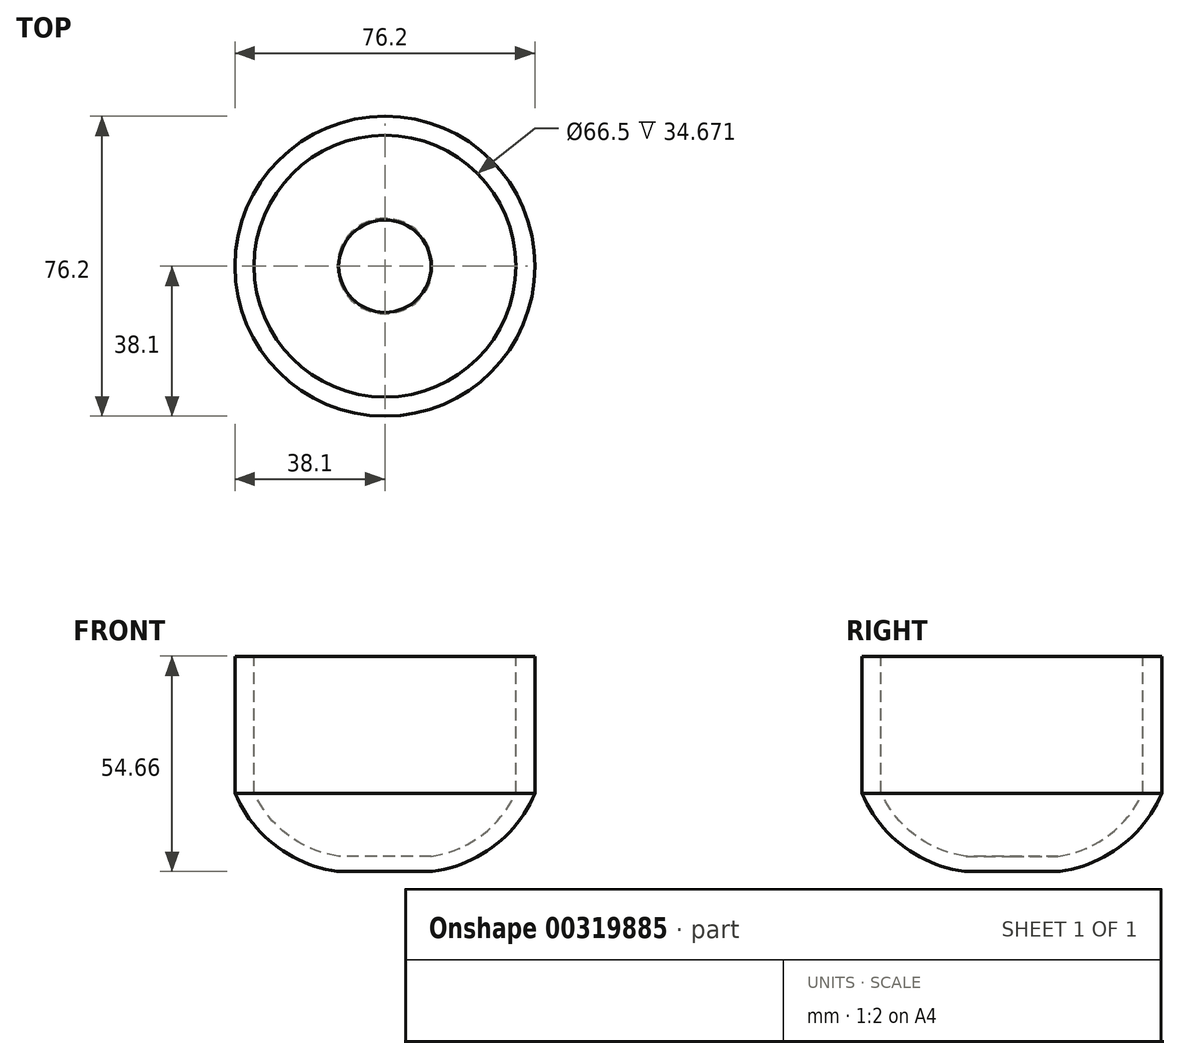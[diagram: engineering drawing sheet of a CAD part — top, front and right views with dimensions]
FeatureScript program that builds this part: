
annotation { "Feature Type Name" : "Feature", "Feature Type Description" : "" }
export const myFeature = defineFeature(function(context is Context, id is Id, definition is map)
    precondition{}
    {
        {
            var Q0;
            Q0=qCreatedBy(makeId("Front.planeOp"),FACE);
            var sketch = newSketch(context, id + "F0", { "sketchPlane" : qUnion([Q0])});
            skLineSegment(sketch, "E0", {"start": v(0, -23.69) * mm, "end": v(0, 30.97) * mm});
            skLineSegment(sketch, "E1", {"start": v(0, 30.97) * mm, "end": v(-38.1, 30.97) * mm});
            skLineSegment(sketch, "E2", {"start": v(-38.1, 30.97) * mm, "end": v(-38.1, -3.85) * mm});
            skArc(sketch, "E3", {"start": v(-38.1, -3.85) * mm, "mid": v(-27.75, -17.22) * mm, "end": v(-12.13, -23.69) * mm});
            skLineSegment(sketch, "E4", {"start": v(-12.13, -23.69) * mm, "end": v(0, -23.69) * mm});
            skSolve(sketch);
        }
        {
            var Q0;
            Q0 = qSketchRegion(id + "F0", true);
            var Q1;
            Q1=sQuery(id+"F0.wireOp",EDGE,"E0");
            revolve(context, id + "F1", {"entities" : qUnion([Q0]), "axis" : qUnion([Q1]), "revolveType" : RevolveType.FULL});
        }
        {
            var Q0;
            Q0=qCreatedBy(makeId("Front.planeOp"),FACE);
            var sketch = newSketch(context, id + "F2", { "sketchPlane" : qUnion([Q0])});
            skLineSegment(sketch, "E5", {"start": v(0, -19.89) * mm, "end": v(0, 30.97) * mm});
            skLineSegment(sketch, "E6", {"start": v(0, 30.97) * mm, "end": v(-33.25, 30.97) * mm});
            skLineSegment(sketch, "E7", {"start": v(-33.25, 30.97) * mm, "end": v(-33.25, -3.7) * mm});
            skArc(sketch, "E8", {"start": v(-33.25, -3.7) * mm, "mid": v(-24.58, -14.57) * mm, "end": v(-11.74, -19.89) * mm});
            skLineSegment(sketch, "E9", {"start": v(-11.74, -19.89) * mm, "end": v(0, -19.89) * mm});
            skSolve(sketch);
        }
        {
            var Q0;
            Q0 = qSketchRegion(id + "F2", true);
            var Q1;
            Q1=sQuery(id+"F2.wireOp",EDGE,"E5");
            revolve(context, id + "F3", {"operationType" : NewBodyOperationType.REMOVE, "entities" : qUnion([Q0]), "axis" : qUnion([Q1]), "revolveType" : RevolveType.FULL, "oppositeDirection" : true});
        }
    });
